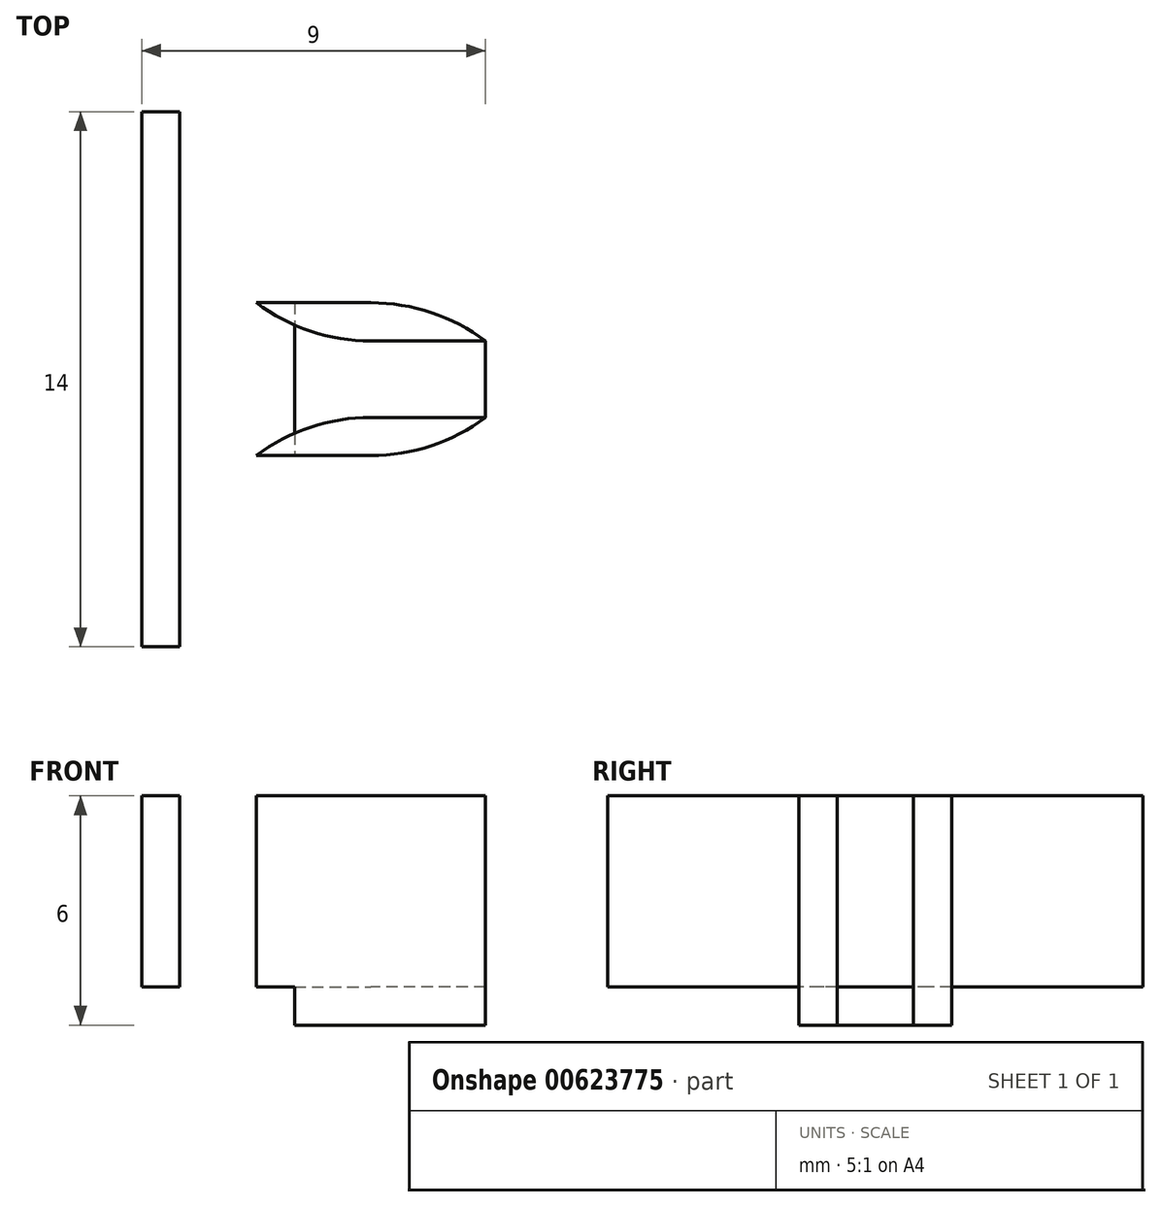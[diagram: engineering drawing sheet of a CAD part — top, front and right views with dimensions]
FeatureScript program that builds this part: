
annotation { "Feature Type Name" : "Feature", "Feature Type Description" : "" }
export const myFeature = defineFeature(function(context is Context, id is Id, definition is map)
    precondition{}
    {
        {
            var Q0;
            Q0=qCreatedBy(makeId("Top.planeOp"),FACE);
            var sketch = newSketch(context, id + "F0", { "sketchPlane" : qUnion([Q0])});
            skLineSegment(sketch, "E0.bottom", {"start": v(4.5, -7) * mm, "end": v(-4.5, -7) * mm});
            skLineSegment(sketch, "E0.top", {"start": v(4.5, 7) * mm, "end": v(-4.5, 7) * mm});
            skLineSegment(sketch, "E0.left", {"start": v(4.5, -7) * mm, "end": v(4.5, 7) * mm});
            skLineSegment(sketch, "E0.right", {"start": v(-4.5, -7) * mm, "end": v(-4.5, 7) * mm});
            skPoint(sketch, "E0.middle", {"position": v(0, 0) * mm});
            skLineSegment(sketch, "E1.bottom", {"start": v(-4.5, 7) * mm, "end": v(-0.5, 7) * mm});
            skLineSegment(sketch, "E1.top", {"start": v(-4.5, -7) * mm, "end": v(-0.5, -7) * mm});
            skLineSegment(sketch, "E1.left", {"start": v(-4.5, 7) * mm, "end": v(-4.5, -7) * mm});
            skLineSegment(sketch, "E1.right", {"start": v(-0.5, 7) * mm, "end": v(-0.5, -7) * mm});
            skLineSegment(sketch, "E2.bottom", {"start": v(4.5, 2) * mm, "end": v(-0.5, 2) * mm});
            skLineSegment(sketch, "E2.top", {"start": v(4.5, -2) * mm, "end": v(-0.5, -2) * mm});
            skLineSegment(sketch, "E2.left", {"start": v(4.5, 2) * mm, "end": v(4.5, -2) * mm});
            skLineSegment(sketch, "E2.right", {"start": v(-0.5, 2) * mm, "end": v(-0.5, -2) * mm});
            skLineSegment(sketch, "E3", {"start": v(3.28, 0) * mm, "end": v(3.28, 2) * mm, "construction": true});
            skSolve(sketch);
        }
        {
            var Q0;
            {var subQ1=sQuery(id+"F0.wireOp",EDGE,"E1.bottom");Q0=makeQuery(id+"F0.imprint","IMPRINT",FACE,{"disambiguationData":[TD([[makeQuery(id+"F0.imprint","IMPRINT",EDGE,{"derivedFrom":subQ1}),-1.0]])]});}
            var Q1;
            Q1=makeQuery(id+"F0.imprint","IMPRINT",FACE,{"disambiguationData":[TD([[makeQuery(id+"F0.imprint","IMPRINT",EDGE,{"derivedFrom":sQuery(id+"F0.wireOp",EDGE,"E2.bottom")}),1.0]])]});
            extrude(context, id + "F1", {"entities" : qUnion([Q0, Q1]), "depth" : 1 * mm, "offsetDistance" : 25 * mm});
        }
        {
            var Q0;
            Q0=makeQuery(id+"F1.opExtrude","CAP_FACE",FACE,{"disambiguationData":[OSD([sQuery(id+"F0.wireOp",EDGE,"E1.bottom"),sQuery(id+"F0.wireOp",EDGE,"E1.top"),sQuery(id+"F0.wireOp",EDGE,"E1.left"),sQuery(id+"F0.wireOp",EDGE,"E1.right"),sQuery(id+"F0.wireOp",EDGE,"E2.bottom"),sQuery(id+"F0.wireOp",EDGE,"E2.top"),sQuery(id+"F0.wireOp",EDGE,"E2.left")])],"isStart":false});
            var sketch = newSketch(context, id + "F2", { "sketchPlane" : qUnion([Q0])});
            skLineSegment(sketch, "E4.bottom", {"start": v(4.5, -2) * mm, "end": v(-1.5, -2) * mm});
            skLineSegment(sketch, "E4.top", {"start": v(4.5, -1) * mm, "end": v(-1.5, -1) * mm});
            skLineSegment(sketch, "E4.left", {"start": v(4.5, -2) * mm, "end": v(4.5, -1) * mm});
            skLineSegment(sketch, "E4.right", {"start": v(-1.5, -2) * mm, "end": v(-1.5, -1) * mm});
            skLineSegment(sketch, "E5.bottom", {"start": v(-1.5, -2) * mm, "end": v(-0.5, -2) * mm});
            skLineSegment(sketch, "E5.top", {"start": v(-1.5, -7) * mm, "end": v(-0.5, -7) * mm});
            skLineSegment(sketch, "E5.left", {"start": v(-1.5, -2) * mm, "end": v(-1.5, -7) * mm});
            skLineSegment(sketch, "E5.right", {"start": v(-0.5, -2) * mm, "end": v(-0.5, -7) * mm});
            skLineSegment(sketch, "E6.bottom", {"start": v(4.5, 2) * mm, "end": v(-1.5, 2) * mm});
            skLineSegment(sketch, "E6.top", {"start": v(4.5, 1) * mm, "end": v(-1.5, 1) * mm});
            skLineSegment(sketch, "E6.left", {"start": v(4.5, 2) * mm, "end": v(4.5, 1) * mm});
            skLineSegment(sketch, "E6.right", {"start": v(-1.5, 2) * mm, "end": v(-1.5, 1) * mm});
            skLineSegment(sketch, "E7.bottom", {"start": v(-1.5, 2) * mm, "end": v(-0.5, 2) * mm});
            skLineSegment(sketch, "E7.top", {"start": v(-1.5, 7) * mm, "end": v(-0.5, 7) * mm});
            skLineSegment(sketch, "E7.left", {"start": v(-1.5, 2) * mm, "end": v(-1.5, 7) * mm});
            skLineSegment(sketch, "E7.right", {"start": v(-0.5, 2) * mm, "end": v(-0.5, 7) * mm});
            skLineSegment(sketch, "E8.bottom", {"start": v(-4.5, 7) * mm, "end": v(-3.5, 7) * mm});
            skLineSegment(sketch, "E8.top", {"start": v(-4.5, -7) * mm, "end": v(-3.5, -7) * mm});
            skLineSegment(sketch, "E8.left", {"start": v(-4.5, 7) * mm, "end": v(-4.5, -7) * mm});
            skLineSegment(sketch, "E8.right", {"start": v(-3.5, 7) * mm, "end": v(-3.5, -7) * mm});
            skSolve(sketch);
        }
        {
            var Q0;
            Q0=makeQuery(id+"F2.imprint","IMPRINT",FACE,{"disambiguationData":[TD([[makeQuery(id+"F2.imprint","IMPRINT",EDGE,{"derivedFrom":sQuery(id+"F2.wireOp",EDGE,"E4.bottom")}),-1.0]])]});
            var Q1;
            Q1=makeQuery(id+"F2.imprint","IMPRINT",FACE,{"disambiguationData":[TD([[makeQuery(id+"F2.imprint","IMPRINT",EDGE,{"derivedFrom":sQuery(id+"F2.wireOp",EDGE,"E5.bottom")}),-1.0]])]});
            var Q2;
            Q2=makeQuery(id+"F2.imprint","IMPRINT",FACE,{"disambiguationData":[TD([[makeQuery(id+"F2.imprint","IMPRINT",EDGE,{"derivedFrom":sQuery(id+"F2.wireOp",EDGE,"E6.bottom")}),1.0]])]});
            var Q3;
            Q3=makeQuery(id+"F2.imprint","IMPRINT",FACE,{"disambiguationData":[TD([[makeQuery(id+"F2.imprint","IMPRINT",EDGE,{"derivedFrom":sQuery(id+"F2.wireOp",EDGE,"E7.bottom")}),1.0]])]});
            extrude(context, id + "F3", {"entities" : qUnion([Q0, Q1, Q2, Q3]), "operationType" : NewBodyOperationType.ADD, "depth" : 5 * mm, "offsetDistance" : 25 * mm});
        }
        {
            var Q0;
            Q0=makeQuery(id+"F3.boolean.opBoolean","MERGE",EDGE,{"derivedFrom":[makeQuery(id+"F1.opExtrude","SWEPT_EDGE",EDGE,{"disambiguationData":[OSD([sQuery(id+"F0.wireOp",EDGE,"E1.right"),sQuery(id+"F0.wireOp",EDGE,"E2.top"),sQuery(id+"F0.wireOp",EDGE,"E2.right")])]}),makeQuery(id+"F3.opExtrude","SWEPT_EDGE",EDGE,{"disambiguationData":[OSD([sQuery(id+"F2.wireOp",EDGE,"E4.bottom"),sQuery(id+"F2.wireOp",EDGE,"E5.bottom"),sQuery(id+"F2.wireOp",EDGE,"E5.right")])]})]});
            var Q1;
            Q1=makeQuery(id+"F3.opExtrude","SWEPT_EDGE",EDGE,{"disambiguationData":[OSD([sQuery(id+"F2.wireOp",EDGE,"E6.top"),sQuery(id+"F2.wireOp",EDGE,"E6.right")])]});
            var Q2;
            Q2=makeQuery(id+"F3.opExtrude","SWEPT_EDGE",EDGE,{"disambiguationData":[OSD([sQuery(id+"F2.wireOp",EDGE,"E4.top"),sQuery(id+"F2.wireOp",EDGE,"E4.right")])]});
            var Q3;
            Q3=makeQuery(id+"F3.boolean.opBoolean","MERGE",EDGE,{"derivedFrom":[makeQuery(id+"F1.opExtrude","SWEPT_EDGE",EDGE,{"disambiguationData":[OSD([sQuery(id+"F0.wireOp",EDGE,"E1.right"),sQuery(id+"F0.wireOp",EDGE,"E2.bottom"),sQuery(id+"F0.wireOp",EDGE,"E2.right")])]}),makeQuery(id+"F3.opExtrude","SWEPT_EDGE",EDGE,{"disambiguationData":[OSD([sQuery(id+"F2.wireOp",EDGE,"E6.bottom"),sQuery(id+"F2.wireOp",EDGE,"E7.bottom"),sQuery(id+"F2.wireOp",EDGE,"E7.right")])]})]});
            fillet(context, id + "F4", {"entities" : qUnion([Q0, Q1, Q2, Q3]), "radius" : 5 * mm, "tangentPropagation" : true, "allowEdgeOverflow" : false});
        }
        {
            var Q0;
            Q0=makeQuery(id+"F2.imprint","IMPRINT",FACE,{"disambiguationData":[TD([[makeQuery(id+"F2.imprint","IMPRINT",EDGE,{"derivedFrom":sQuery(id+"F2.wireOp",EDGE,"E8.bottom")}),-1.0]])]});
            extrude(context, id + "F5", {"entities" : qUnion([Q0]), "operationType" : NewBodyOperationType.ADD, "depth" : 5 * mm, "offsetDistance" : 25 * mm});
        }
    });
